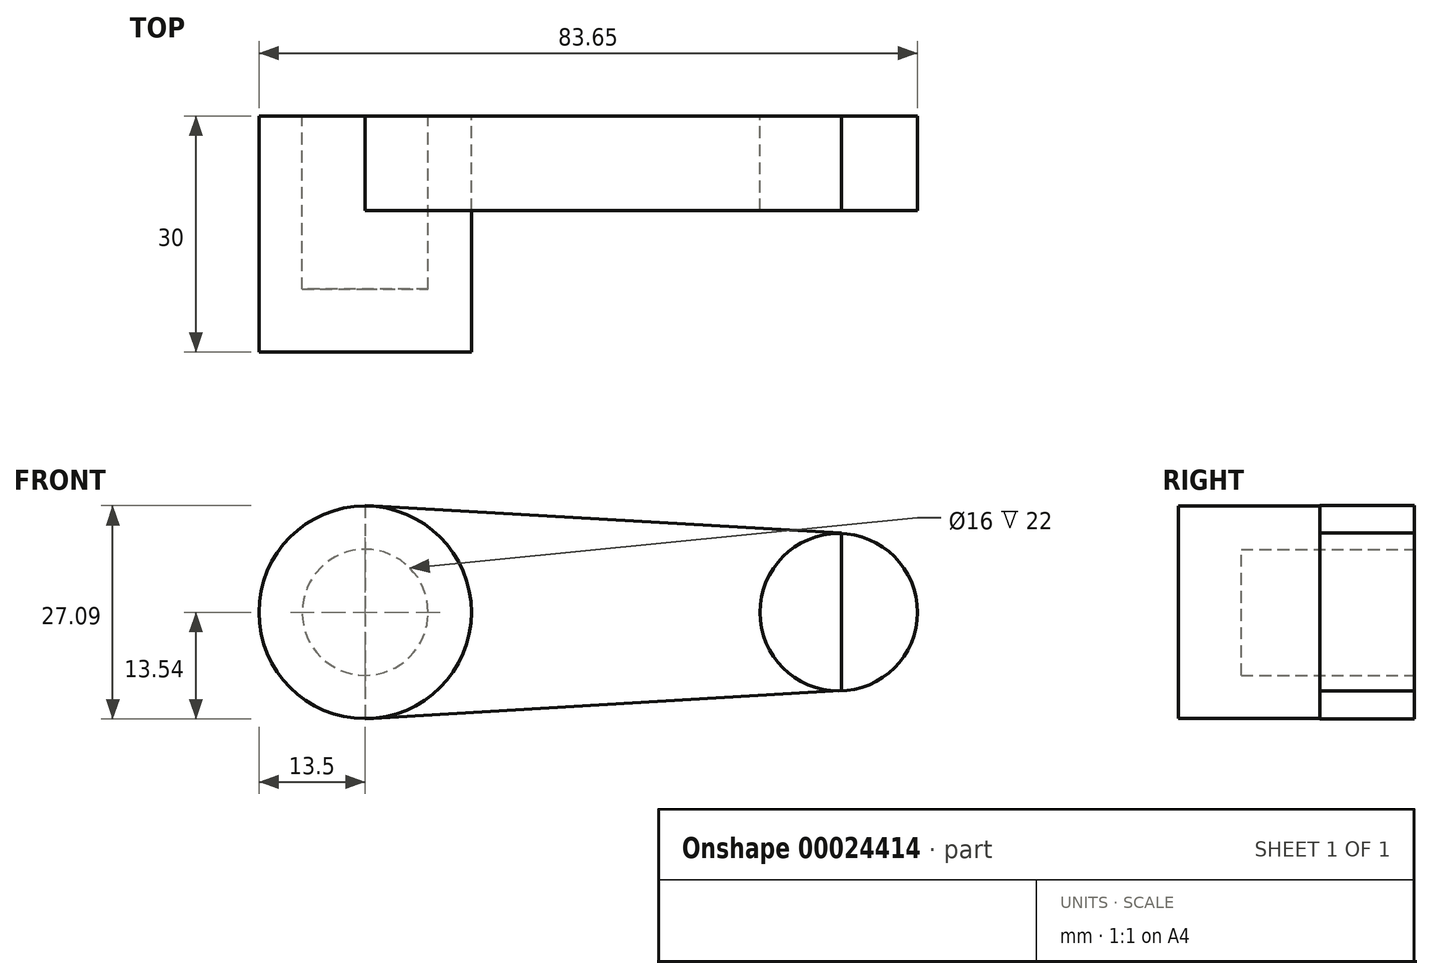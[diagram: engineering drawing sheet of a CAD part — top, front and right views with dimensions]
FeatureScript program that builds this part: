
annotation { "Feature Type Name" : "Feature", "Feature Type Description" : "" }
export const myFeature = defineFeature(function(context is Context, id is Id, definition is map)
    precondition{}
    {
        {
            var Q0;
            Q0=qCreatedBy(makeId("Front.planeOp"),FACE);
            var sketch = newSketch(context, id + "F0", { "sketchPlane" : qUnion([Q0])});
            skCircle(sketch, "E0", {"center": v(0, 0) * mm, "radius": 13.5 * mm});
            skSolve(sketch);
        }
        {
            var Q0;
            Q0 = qSketchRegion(id + "F0", true);
            extrude(context, id + "F1", {"entities" : qUnion([Q0]), "depth" : 30 * mm});
        }
        {
            var Q0;
            Q0=qCreatedBy(makeId("Front.planeOp"),FACE);
            var sketch = newSketch(context, id + "F2", { "sketchPlane" : qUnion([Q0])});
            skCircle(sketch, "E1", {"center": v(0, 0) * mm, "radius": 8 * mm});
            skSolve(sketch);
        }
        {
            var Q0;
            Q0 = qSketchRegion(id + "F2", true);
            var Q1;
            Q1=makeQuery(id+"F1.opExtrude","CAP_FACE",FACE,{"disambiguationData":[OSD([sQuery(id+"F0.wireOp",EDGE,"E0")])],"isStart":false});
            extrude(context, id + "F3", {"entities" : qUnion([Q0, Q1]), "operationType" : NewBodyOperationType.REMOVE, "depth" : 22 * mm});
        }
        {
            var Q0;
            Q0=qCreatedBy(makeId("Front.planeOp"),FACE);
            var sketch = newSketch(context, id + "F4", { "sketchPlane" : qUnion([Q0])});
            skCircle(sketch, "E2", {"center": v(60.15, 0) * mm, "radius": 10 * mm});
            skSolve(sketch);
        }
        {
            var Q0;
            Q0 = qSketchRegion(id + "F4", true);
            extrude(context, id + "F5", {"entities" : qUnion([Q0]), "depth" : 12 * mm});
        }
        {
            var Q0;
            Q0=qCreatedBy(makeId("Front.planeOp"),FACE);
            var sketch = newSketch(context, id + "F6", { "sketchPlane" : qUnion([Q0])});
            skLineSegment(sketch, "E3", {"start": v(60.47, 10.06) * mm, "end": v(0, 13.55) * mm});
            skLineSegment(sketch, "E4", {"start": v(60.47, -9.94) * mm, "end": v(0, -13.54) * mm});
            skLineSegment(sketch, "E5", {"start": v(60.47, 10.06) * mm, "end": v(60.47, -9.94) * mm});
            skLineSegment(sketch, "E6", {"start": v(0, 13.55) * mm, "end": v(0, -13.54) * mm});
            skSolve(sketch);
        }
        {
            var Q0;
            Q0=makeQuery(id+"F6.imprint","IMPRINT",FACE,{"disambiguationData":[TD([[makeQuery(id+"F6.imprint","IMPRINT",EDGE,{"derivedFrom":sQuery(id+"F6.wireOp",EDGE,"E3")}),1.0]])]});
            extrude(context, id + "F7", {"entities" : qUnion([Q0]), "depth" : 12 * mm});
        }
    });
